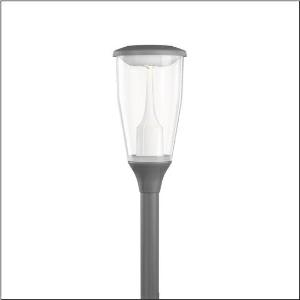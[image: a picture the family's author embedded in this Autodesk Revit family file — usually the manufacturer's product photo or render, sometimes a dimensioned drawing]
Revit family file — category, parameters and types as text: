
# Revit family: dl_11_iq___p1_0a_5xa5565bf14hp00022_ddba
name_source: partatom
category: Lighting Fixtures
units: mm (PartAtom-declared; Revit-internal decimal feet)

## family parameters
Cut with Voids When Loaded = No
Host = Face
Light Source = No
Part Type = Normal
Room Calculation Point = No
Round Connector Dimension = Use Diameter
Shared = No

## types (1)
- --- (1 x LED, 3950 lm, 33.6 W, 2200K)
    Apparent Load = 34 VA
    CIE Flux Codes = 33 63 91 94 100
    Color Rendering = 70
    Color Temperature = 2200K
    Default Elevation = 1800 mm
    Description = DL 11 iQ, mast luminaire, Module 540 iQ-SR, primary light control with 3 zone facetted reflector, of plastic, silver coated, highly specular, structured, primary optical cover: cover, of PMMA, transparent, light distribution: P1.0a, light emission: direct distribution, primary light characteristic: asymmetric, installation type: post-top, LED, High Power LED, light colour: 722, colour temperature: 2200K, control: Street-Remote, Auto-Match, Temp-Guard, Lumen-Switch, Night-Set, Smart-Wire, Light-Fading, Desk-Remote (wireless, voltage-free reading and setting of iQ features in the workshop via application-optimized NFC function/RFID function), optimised constant luminous flux control (CLO 2.0), mains connection: 220..240V, AC, 50/60Hz, connection cable pre-assembled, cable length: 5,5m, start of lifetime: 34W, end of service life: 36W, luminaire housing, upper part, of diecast aluminium, coated, Siteco® metallic grey (DB 702S), spigot size: 60mm (post-top), post-top mast mounting element, of diecast aluminium, coated, Siteco® metallic grey (DB 702S), Module 540 iQ-SR, traffic white (RAL 9016), equipment: Power, protection rating (complete): IP66, insulation class (complete): insulation class II (safety insulation), certification: CE, ENEC, ENEC+, VDE, packaging unit: 1 piece

Light Distribution: P1.0a
    Height = 665 mm
    Lamp = 1 x LED
    Lamp Light Flux = 3950 lm
    Lamp Power = 33.6 W
    Lamp count = 1
    Length = 334 mm
    Luminous efficacy = 118 lm/W
    Manufacturer = Siteco
    ModVariant = No
    Model = 5XA5565BF14HP00022
    Number of Poles = 1
    OnlyDefault = Yes
    Power Factor = 1
    Product Name = DL 11 iQ | P1.0a
    Product group = mast luminaire | pylon top
    ProductGroupID = 6100
    Protection Class = Protection class II
    Protection Degree = IP 66
    RLX_Detail_Level = 1
    RLX_Emergency_Light_Flux = 0 lm
    RLX_Emergency_Type = 0
    RLX_Emergency_Type_DB = No
    RlxData = <blob elided: 104893 chars, md5=26c3a9cc>
    Socket = socket
    Standby Power = 0 W
    System Light Flux = 3950 lm
    System Power = 34 W
    Type Comments = factory setting: luminous flux: 100 % | dim-lin: 254 | 695 mA
    Type Image = l_1258354.jpg
    URL = http://relux.com
    VarID = @adj_001851
    Voltage = 0 V
    Weight = 0.00 kg
    Width = 0 mm  [stored 0 ft]

note: [stored X ft] marks values corroborated as IEEE doubles in the binary element streams (Revit-internal decimal feet)

## geometry (parser evidence)
native form markers: Blend x4, Sweep x10
no freeform markers — native parametric forms only
